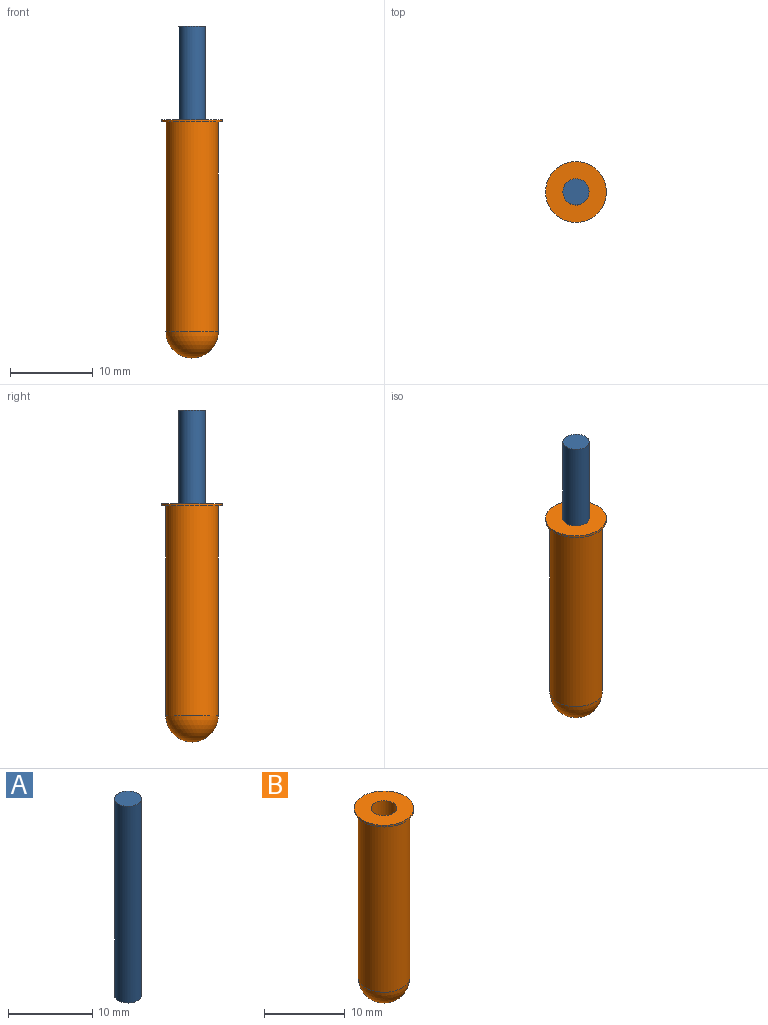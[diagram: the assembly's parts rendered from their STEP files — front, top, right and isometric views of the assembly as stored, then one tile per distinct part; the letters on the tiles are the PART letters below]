
ASSEMBLY  parts=2 mates=1
PART A: 3 faces, bbox 3.2x3.2x28.6 mm
  f0: cylinder r=1.59mm len=28.58mm, axis (0,0,-1), area 285mm2, adj f1,f2
  f1: plane 3.18x3.18mm, normal (0,0,1), area 7.9mm2, adj f0
  f2: plane 3.18x3.18mm, normal (0,0,-1), area 7.9mm2, adj f0
PART B: 7 faces, bbox 7.4x7.4x28.8 mm
  f0: cylinder r=3.17mm len=25.4mm, axis (0,0,1), area 506.7mm2, adj f1,f6
  f1: sphere r=3.17mm, area 63.3mm2, adj f0
  f2: sphere r=1.59mm, area 15.8mm2, adj f3
  f3: cylinder r=1.59mm len=25.65mm, axis (0,0,1), area 255.9mm2, adj f2,f4
  f4: plane 7.37x7.37mm, normal (0,0,1), area 34.7mm2, adj f3,f5
  f5: cylinder r=3.68mm len=7.37mm, axis (0,0,1), area 5.9mm2, adj f4,f6
  f6: plane 7.37x7.37mm, normal (0,0,-1), area 10.9mm2, adj f0,f5
PLACE A t=(-0.98,1.93,-0.77)mm
PLACE B t=(-0.98,1.93,3.52)mm fixed
MATE slider A.f0 <-> B.f0  axis (0,0,-1) through (-0.98,1.93,13.52)mm
